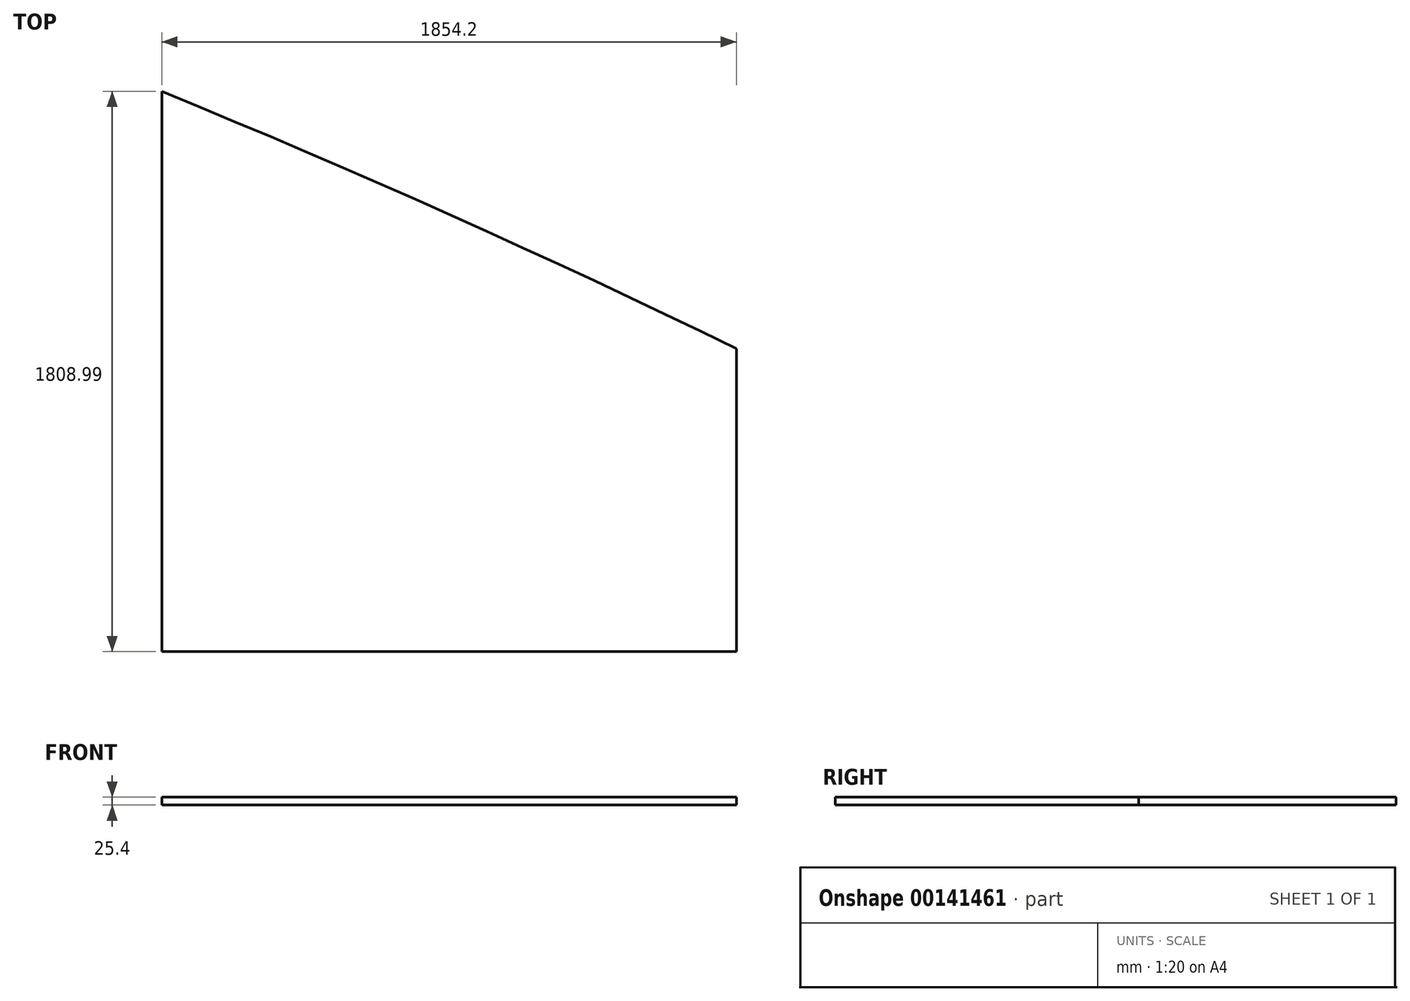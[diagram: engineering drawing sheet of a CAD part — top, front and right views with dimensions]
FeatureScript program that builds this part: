
annotation { "Feature Type Name" : "Feature", "Feature Type Description" : "" }
export const myFeature = defineFeature(function(context is Context, id is Id, definition is map)
    precondition{}
    {
        {
            var Q0;
            Q0=qCreatedBy(makeId("Top.planeOp"),FACE);
            var sketch = newSketch(context, id + "F0", { "sketchPlane" : qUnion([Q0])});
            skLineSegment(sketch, "E0", {"start": v(-953.4, 318.56) * mm, "end": v(900.8, 318.56) * mm});
            skLineSegment(sketch, "E1", {"start": v(-953.4, 318.56) * mm, "end": v(-953.4, 2127.55) * mm});
            skLineSegment(sketch, "E2", {"start": v(900.8, 318.56) * mm, "end": v(900.8, 1297.22) * mm});
            skLineSegment(sketch, "E3", {"start": v(-26.3, 318.56) * mm, "end": v(-26.3, 1730.29) * mm});
            skArc(sketch, "E4", {"start": v(900.8, 1297.22) * mm, "mid": v(-19.61, 1727.3) * mm, "end": v(-953.4, 2127.55) * mm});
            skSolve(sketch);
        }
        {
            var Q0;
            {var subQ0=sQuery(id+"F0.wireOp",EDGE,"E1");Q0=makeQuery(id+"F0.imprint","IMPRINT",FACE,{"disambiguationData":[TD([[makeQuery(id+"F0.imprint","IMPRINT",EDGE,{"derivedFrom":subQ0}),-1.0]])]});}
            var Q1;
            {var subQ0=sQuery(id+"F0.wireOp",EDGE,"E2");Q1=makeQuery(id+"F0.imprint","IMPRINT",FACE,{"disambiguationData":[TD([[makeQuery(id+"F0.imprint","IMPRINT",EDGE,{"derivedFrom":subQ0}),1.0]])]});}
            extrude(context, id + "F1", {"entities" : qUnion([Q0, Q1]), "depth" : 25.4 * mm});
        }
    });
